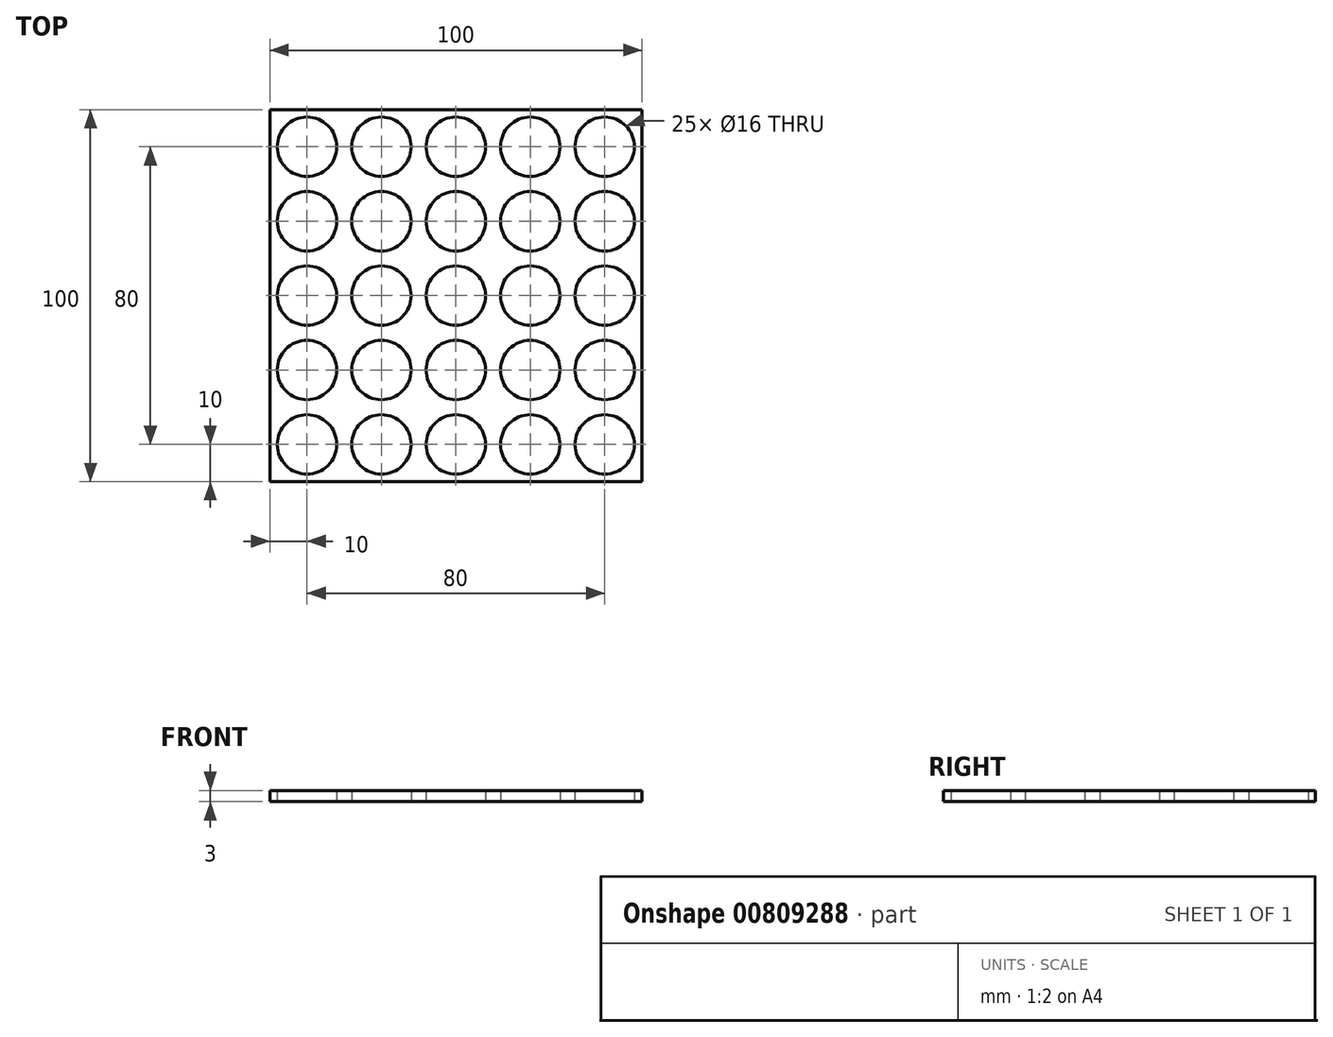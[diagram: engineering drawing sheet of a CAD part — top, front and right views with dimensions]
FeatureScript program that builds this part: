
annotation { "Feature Type Name" : "Feature", "Feature Type Description" : "" }
export const myFeature = defineFeature(function(context is Context, id is Id, definition is map)
    precondition{}
    {
        {
            var Q0;
            Q0=qCreatedBy(makeId("Top.planeOp"),FACE);
            var sketch = newSketch(context, id + "F0", { "sketchPlane" : qUnion([Q0])});
            skLineSegment(sketch, "E0.bottom", {"start": v(50, 50) * mm, "end": v(-50, 50) * mm});
            skLineSegment(sketch, "E0.top", {"start": v(50, -50) * mm, "end": v(-50, -50) * mm});
            skLineSegment(sketch, "E0.left", {"start": v(50, 50) * mm, "end": v(50, -50) * mm});
            skLineSegment(sketch, "E0.right", {"start": v(-50, 50) * mm, "end": v(-50, -50) * mm});
            skPoint(sketch, "E0.middle", {"position": v(0, 0) * mm});
            skCircle(sketch, "E1", {"center": v(0, 0) * mm, "radius": 8 * mm});
            skCircle(sketch, "E2.0.1.0", {"center": v(0, 20) * mm, "radius": 8 * mm});
            skCircle(sketch, "E2.0.2.0", {"center": v(0, 40) * mm, "radius": 8 * mm});
            skCircle(sketch, "E2.1.0.0", {"center": v(20, 0) * mm, "radius": 8 * mm});
            skCircle(sketch, "E2.1.1.0", {"center": v(20, 20) * mm, "radius": 8 * mm});
            skCircle(sketch, "E2.1.2.0", {"center": v(20, 40) * mm, "radius": 8 * mm});
            skCircle(sketch, "E2.2.0.0", {"center": v(40, 0) * mm, "radius": 8 * mm});
            skCircle(sketch, "E2.2.1.0", {"center": v(40, 20) * mm, "radius": 8 * mm});
            skCircle(sketch, "E2.2.2.0", {"center": v(40, 40) * mm, "radius": 8 * mm});
            skLineSegment(sketch, "E2.direction1", {"start": v(0, 0) * mm, "end": v(20, 0) * mm, "construction": true});
            skLineSegment(sketch, "E2.direction2", {"start": v(0, 0) * mm, "end": v(0, 20) * mm, "construction": true});
            skCircle(sketch, "E3.MirrorC", {"center": v(-20, 20) * mm, "radius": 8 * mm});
            skCircle(sketch, "E4.MirrorC", {"center": v(-40, 20) * mm, "radius": 8 * mm});
            skCircle(sketch, "E5.MirrorC", {"center": v(-40, 40) * mm, "radius": 8 * mm});
            skCircle(sketch, "E6.MirrorC", {"center": v(-20, 40) * mm, "radius": 8 * mm});
            skCircle(sketch, "E7.MirrorC", {"center": v(-40, 0) * mm, "radius": 8 * mm});
            skCircle(sketch, "E8.MirrorC", {"center": v(-20, 0) * mm, "radius": 8 * mm});
            skCircle(sketch, "E9.MirrorC", {"center": v(-40, -20) * mm, "radius": 8 * mm});
            skCircle(sketch, "E10.MirrorC", {"center": v(-40, -40) * mm, "radius": 8 * mm});
            skCircle(sketch, "E11.MirrorC", {"center": v(-20, -40) * mm, "radius": 8 * mm});
            skCircle(sketch, "E12.MirrorC", {"center": v(0, -20) * mm, "radius": 8 * mm});
            skCircle(sketch, "E13.MirrorC", {"center": v(-20, -20) * mm, "radius": 8 * mm});
            skCircle(sketch, "E14.MirrorC", {"center": v(40, -20) * mm, "radius": 8 * mm});
            skCircle(sketch, "E15.MirrorC", {"center": v(20, -20) * mm, "radius": 8 * mm});
            skLineSegment(sketch, "E16.MirrorCS", {"start": v(0, 0) * mm, "end": v(0, -20) * mm, "construction": true});
            skCircle(sketch, "E17.MirrorC", {"center": v(0, -40) * mm, "radius": 8 * mm});
            skCircle(sketch, "E18.MirrorC", {"center": v(20, -40) * mm, "radius": 8 * mm});
            skCircle(sketch, "E19.MirrorC", {"center": v(40, -40) * mm, "radius": 8 * mm});
            skSolve(sketch);
        }
        {
            var Q0;
            Q0=makeQuery(id+"F0.imprint","IMPRINT",FACE,{"disambiguationData":[TD([[makeQuery(id+"F0.imprint","IMPRINT",EDGE,{"derivedFrom":sQuery(id+"F0.wireOp",EDGE,"E0.bottom")}),1.0]])]});
            extrude(context, id + "F1", {"entities" : qUnion([Q0]), "depth" : 3 * mm, "offsetDistance" : 25 * mm});
        }
    });
